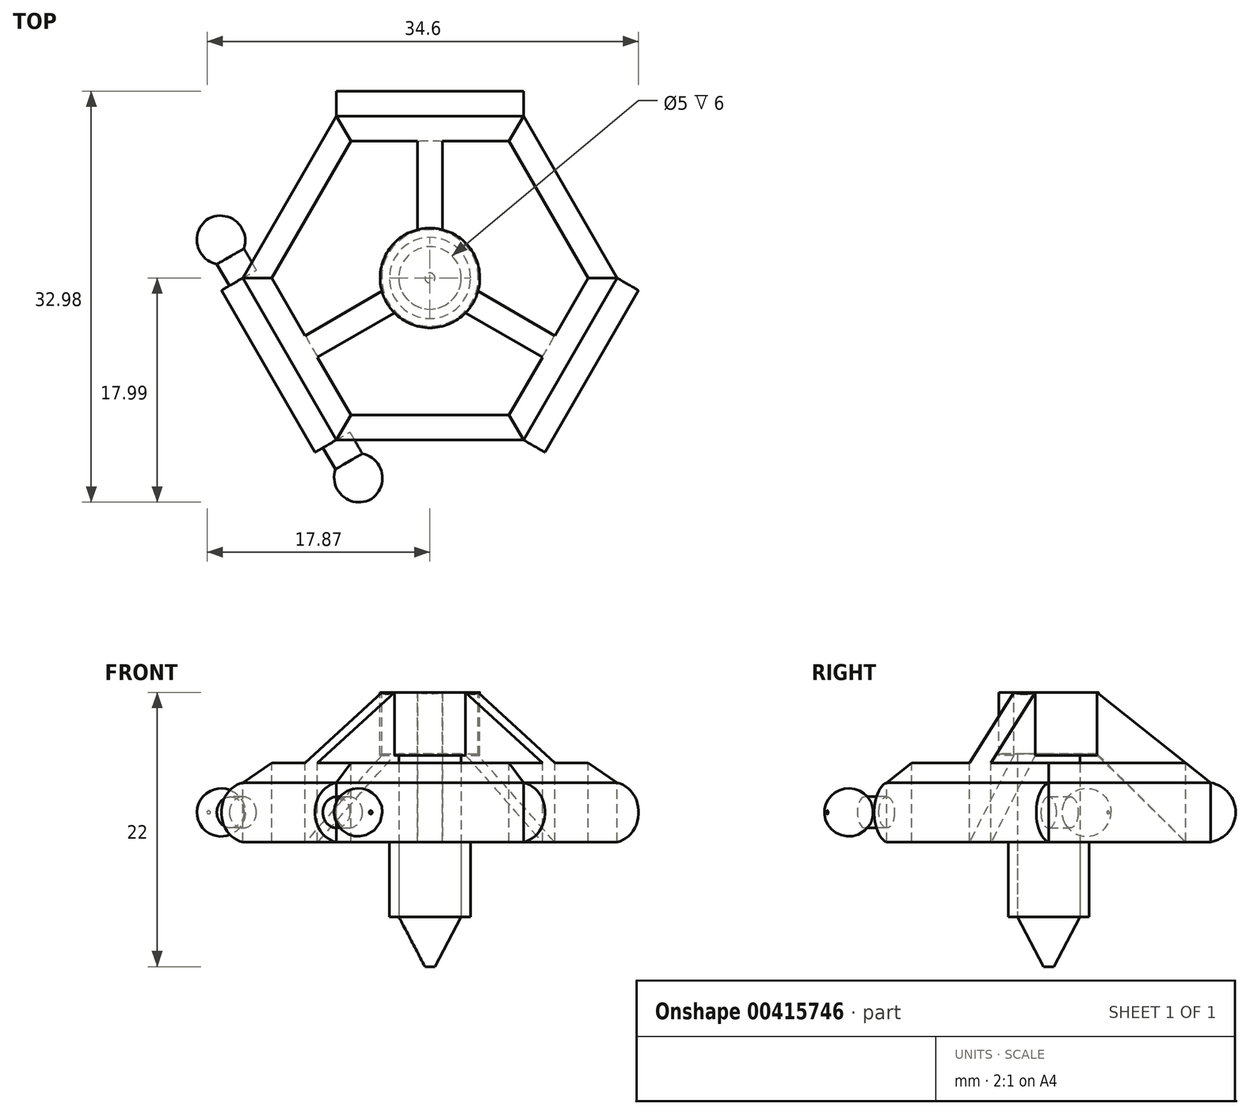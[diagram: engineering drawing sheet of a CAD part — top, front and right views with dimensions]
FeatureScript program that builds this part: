
annotation { "Feature Type Name" : "Feature", "Feature Type Description" : "" }
export const myFeature = defineFeature(function(context is Context, id is Id, definition is map)
    precondition{}
    {
        {
            var Q0;
            Q0=qCreatedBy(makeId("Top.planeOp"),FACE);
            var sketch = newSketch(context, id + "F0", { "sketchPlane" : qUnion([Q0])});
            skLineSegment(sketch, "E0", {"start": v(0, 25.98) * mm, "end": v(-22.5, -13) * mm, "construction": true});
            skLineSegment(sketch, "E1", {"start": v(-22.5, -13) * mm, "end": v(22.5, -13) * mm, "construction": true});
            skLineSegment(sketch, "E2", {"start": v(22.5, -13) * mm, "end": v(0, 25.98) * mm, "construction": true});
            skLineSegment(sketch, "E3", {"start": v(0, 0) * mm, "end": v(-22.5, -13) * mm, "construction": true});
            skLineSegment(sketch, "E4", {"start": v(0, 0) * mm, "end": v(22.5, -13) * mm, "construction": true});
            skLineSegment(sketch, "E5", {"start": v(0, 0) * mm, "end": v(0, 25.98) * mm, "construction": true});
            skCircle(sketch, "E6.cCircle", {"center": v(0, 0) * mm, "radius": 13 * mm, "construction": true});
            skLineSegment(sketch, "E6.0", {"start": v(7.5, -13) * mm, "end": v(-7.5, -13) * mm});
            skLineSegment(sketch, "E6.1", {"start": v(-7.5, -13) * mm, "end": v(-15, 0) * mm});
            skLineSegment(sketch, "E6.2", {"start": v(-15, 0) * mm, "end": v(-7.5, 13) * mm});
            skLineSegment(sketch, "E6.3", {"start": v(-7.5, 13) * mm, "end": v(7.5, 13) * mm});
            skLineSegment(sketch, "E6.4", {"start": v(7.5, 13) * mm, "end": v(15, 0) * mm});
            skLineSegment(sketch, "E6.5", {"start": v(15, 0) * mm, "end": v(7.5, -13) * mm});
            skPoint(sketch, "E6.0.midPoint", {"position": v(0, -13) * mm});
            skSolve(sketch);
        }
        {
            var Q0;
            Q0=makeQuery(id+"F0.imprint","IMPRINT",FACE,{"disambiguationData":[TD([[makeQuery(id+"F0.imprint","IMPRINT",EDGE,{"derivedFrom":sQuery(id+"F0.wireOp",EDGE,"E6.0")}),-1.0]])]});
            extrude(context, id + "F1", {"entities" : qUnion([Q0]), "depth" : 4.75 * mm});
        }
        {
            var Q0;
            Q0=makeQuery(id+"F1.opExtrude","CAP_FACE",FACE,{"disambiguationData":[OSD([sQuery(id+"F0.wireOp",EDGE,"E6.0"),sQuery(id+"F0.wireOp",EDGE,"E6.1"),sQuery(id+"F0.wireOp",EDGE,"E6.2"),sQuery(id+"F0.wireOp",EDGE,"E6.3"),sQuery(id+"F0.wireOp",EDGE,"E6.4"),sQuery(id+"F0.wireOp",EDGE,"E6.5")])],"isStart":false});
            cPlane(context, id + "F2", {"entities" : qUnion([Q0]), "cplaneType" : CPlaneType.OFFSET, "offset" : 10.33 * mm, "width" : 150 * mm, "height" : 150 * mm});
        }
        {
            var Q0;
            Q0=qCreatedBy(id+"F2.planeOp",FACE);
            var sketch = newSketch(context, id + "F3", { "sketchPlane" : qUnion([Q0])});
            skPoint(sketch, "E7", {"position": v(0, 0) * mm});
            skSolve(sketch);
        }
        {
            var Q1;
            Q1=makeQuery(id+"F1.opExtrude","CAP_FACE",FACE,{"disambiguationData":[OSD([sQuery(id+"F0.wireOp",EDGE,"E6.0"),sQuery(id+"F0.wireOp",EDGE,"E6.1"),sQuery(id+"F0.wireOp",EDGE,"E6.2"),sQuery(id+"F0.wireOp",EDGE,"E6.3"),sQuery(id+"F0.wireOp",EDGE,"E6.4"),sQuery(id+"F0.wireOp",EDGE,"E6.5")])],"isStart":false});
            var Q2;
            Q2=sQuery(id+"F3.wireOp",VERTEX,"E7");
            loft(context, id + "F4", {"operationType" : NewBodyOperationType.ADD, "sheetProfilesArray" : [{ "sheetProfileEntities" : qUnion([Q1]) }, { "sheetProfileEntities" : qUnion([Q2]) }]});
        }
        {
            var Q0;
            Q0=qCreatedBy(id+"F2.planeOp",FACE);
            var sketch = newSketch(context, id + "F5", { "sketchPlane" : qUnion([Q0])});
            skCircle(sketch, "E8", {"center": v(0, 0) * mm, "radius": 4 * mm});
            skLineSegment(sketch, "E9", {"start": v(-7.5, -13) * mm, "end": v(7.5, 13) * mm, "construction": true});
            skLineSegment(sketch, "E10", {"start": v(7.5, -13) * mm, "end": v(-7.5, 13) * mm, "construction": true});
            skLineSegment(sketch, "E11.bottom", {"start": v(-1, 11) * mm, "end": v(1, 11) * mm});
            skLineSegment(sketch, "E11.top", {"start": v(-1, 0) * mm, "end": v(1, 0) * mm});
            skLineSegment(sketch, "E11.left", {"start": v(-1, 11) * mm, "end": v(-1, 0) * mm});
            skLineSegment(sketch, "E11.right", {"start": v(1, 11) * mm, "end": v(1, 0) * mm});
            skLineSegment(sketch, "E12", {"start": v(-0.5, -0.87) * mm, "end": v(0.5, 0.87) * mm});
            skLineSegment(sketch, "E13", {"start": v(0.5, 0.87) * mm, "end": v(10.02, -4.63) * mm});
            skLineSegment(sketch, "E14", {"start": v(10.02, -4.63) * mm, "end": v(9.02, -6.36) * mm});
            skLineSegment(sketch, "E15", {"start": v(9.02, -6.36) * mm, "end": v(-0.5, -0.87) * mm});
            skLineSegment(sketch, "E16", {"start": v(-0.5, 0.87) * mm, "end": v(0.5, -0.87) * mm});
            skLineSegment(sketch, "E17", {"start": v(0.5, -0.87) * mm, "end": v(-9.02, -6.36) * mm});
            skLineSegment(sketch, "E18", {"start": v(-9.02, -6.36) * mm, "end": v(-10.02, -4.63) * mm});
            skLineSegment(sketch, "E19", {"start": v(-10.02, -4.63) * mm, "end": v(-0.5, 0.87) * mm});
            skCircle(sketch, "E20.cCircle", {"center": v(0, 0) * mm, "radius": 11 * mm, "construction": true});
            skLineSegment(sketch, "E20.0", {"start": v(-6.35, 11) * mm, "end": v(6.35, 11) * mm});
            skLineSegment(sketch, "E20.1", {"start": v(6.35, 11) * mm, "end": v(12.7, 0) * mm});
            skLineSegment(sketch, "E20.2", {"start": v(12.7, 0) * mm, "end": v(6.35, -11) * mm});
            skLineSegment(sketch, "E20.3", {"start": v(6.35, -11) * mm, "end": v(-6.35, -11) * mm});
            skLineSegment(sketch, "E20.4", {"start": v(-6.35, -11) * mm, "end": v(-12.7, 0) * mm});
            skLineSegment(sketch, "E20.5", {"start": v(-12.7, 0) * mm, "end": v(-6.35, 11) * mm});
            skPoint(sketch, "E20.0.midPoint", {"position": v(0, 11) * mm});
            skSolve(sketch);
        }
        {
            var Q0;
            {var subQ3=sQuery(id+"F5.wireOp",EDGE,"E20.5");Q0=makeQuery(id+"F5.imprint","IMPRINT",FACE,{"disambiguationData":[TD([[makeQuery(id+"F5.imprint","IMPRINT",EDGE,{"derivedFrom":subQ3}),-1.0]])]});}
            var Q1;
            {var subQ3=sQuery(id+"F5.wireOp",EDGE,"E20.1");Q1=makeQuery(id+"F5.imprint","IMPRINT",FACE,{"disambiguationData":[TD([[makeQuery(id+"F5.imprint","IMPRINT",EDGE,{"derivedFrom":subQ3}),-1.0]])]});}
            var Q2;
            {var subQ3=sQuery(id+"F5.wireOp",EDGE,"E20.3");Q2=makeQuery(id+"F5.imprint","IMPRINT",FACE,{"disambiguationData":[TD([[makeQuery(id+"F5.imprint","IMPRINT",EDGE,{"derivedFrom":subQ3}),-1.0]])]});}
            extrude(context, id + "F6", {"entities" : qUnion([Q0, Q1, Q2]), "operationType" : NewBodyOperationType.REMOVE, "oppositeDirection" : true, "depth" : 25 * mm});
        }
        {
            var Q0;
            {var subQ0=sQuery(id+"F5.wireOp",EDGE,"E11.left");var subQ1=sQuery(id+"F5.wireOp",EDGE,"E8");var subQ2=makeQuery(id+"F5.imprint","INTERSECT",VERTEX,{"derivedFrom":[subQ1,subQ0]});Q0=makeQuery(id+"F5.imprint","IMPRINT",FACE,{"disambiguationData":[TD([[makeQuery(id+"F5.imprint","IMPRINT",EDGE,{"disambiguationData":[TD([[subQ2,-1.0]])],"derivedFrom":subQ1}),1.0]])]});}
            var Q1;
            {var subQ1=sQuery(id+"F5.wireOp",EDGE,"E8");var subQ5=sQuery(id+"F5.wireOp",EDGE,"E11.left");var subQ6=makeQuery(id+"F5.imprint","INTERSECT",VERTEX,{"derivedFrom":[subQ1,subQ5]});Q1=makeQuery(id+"F5.imprint","IMPRINT",FACE,{"disambiguationData":[TD([[makeQuery(id+"F5.imprint","IMPRINT",EDGE,{"disambiguationData":[TD([[subQ6,1.0]])],"derivedFrom":subQ1}),1.0]])]});}
            var Q2;
            {var subQ0=sQuery(id+"F5.wireOp",EDGE,"E11.right");var subQ1=sQuery(id+"F5.wireOp",EDGE,"E8");var subQ2=makeQuery(id+"F5.imprint","INTERSECT",VERTEX,{"derivedFrom":[subQ1,subQ0]});Q2=makeQuery(id+"F5.imprint","IMPRINT",FACE,{"disambiguationData":[TD([[makeQuery(id+"F5.imprint","IMPRINT",EDGE,{"disambiguationData":[TD([[subQ2,1.0]])],"derivedFrom":subQ1}),1.0]])]});}
            var Q3;
            {var subQ8=sQuery(id+"F5.wireOp",EDGE,"E15");var subQ10=sQuery(id+"F5.wireOp",EDGE,"E8");var subQ13=makeQuery(id+"F5.imprint","INTERSECT",VERTEX,{"derivedFrom":[subQ10,subQ8]});Q3=makeQuery(id+"F5.imprint","IMPRINT",FACE,{"disambiguationData":[TD([[makeQuery(id+"F5.imprint","IMPRINT",EDGE,{"disambiguationData":[TD([[subQ13,-1.0]])],"derivedFrom":subQ10}),1.0]])]});}
            var Q4;
            {var subQ6=sQuery(id+"F5.wireOp",EDGE,"E8");var subQ11=sQuery(id+"F5.wireOp",EDGE,"E19");var subQ13=makeQuery(id+"F5.imprint","INTERSECT",VERTEX,{"derivedFrom":[subQ6,subQ11]});Q4=makeQuery(id+"F5.imprint","IMPRINT",FACE,{"disambiguationData":[TD([[makeQuery(id+"F5.imprint","IMPRINT",EDGE,{"disambiguationData":[TD([[subQ13,-1.0]])],"derivedFrom":subQ6}),1.0]])]});}
            var Q5;
            {var subQ0=sQuery(id+"F5.wireOp",EDGE,"E17");var subQ1=sQuery(id+"F5.wireOp",EDGE,"E8");var subQ2=makeQuery(id+"F5.imprint","INTERSECT",VERTEX,{"derivedFrom":[subQ1,subQ0]});Q5=makeQuery(id+"F5.imprint","IMPRINT",FACE,{"disambiguationData":[TD([[makeQuery(id+"F5.imprint","IMPRINT",EDGE,{"disambiguationData":[TD([[subQ2,-1.0]])],"derivedFrom":subQ1}),1.0]])]});}
            var Q6;
            {var subQ0=sQuery(id+"F5.wireOp",EDGE,"E11.right");var subQ1=sQuery(id+"F5.wireOp",EDGE,"E11.top");var subQ2=makeQuery(id+"F5.imprint","INTERSECT",VERTEX,{"derivedFrom":[subQ1,subQ0]});Q6=makeQuery(id+"F5.imprint","IMPRINT",FACE,{"disambiguationData":[TD([[makeQuery(id+"F5.imprint","IMPRINT",EDGE,{"disambiguationData":[TD([[subQ2,1.0]])],"derivedFrom":subQ0}),-1.0]])]});}
            var Q7;
            {var subQ0=sQuery(id+"F5.wireOp",EDGE,"E11.left");var subQ1=sQuery(id+"F5.wireOp",EDGE,"E11.top");var subQ2=makeQuery(id+"F5.imprint","INTERSECT",VERTEX,{"derivedFrom":[subQ1,subQ0]});Q7=makeQuery(id+"F5.imprint","IMPRINT",FACE,{"disambiguationData":[TD([[makeQuery(id+"F5.imprint","IMPRINT",EDGE,{"disambiguationData":[TD([[subQ2,1.0]])],"derivedFrom":subQ0}),1.0]])]});}
            var Q8;
            {var subQ0=sQuery(id+"F5.wireOp",EDGE,"E15");var subQ1=sQuery(id+"F5.wireOp",EDGE,"E12");var subQ2=makeQuery(id+"F5.imprint","INTERSECT",VERTEX,{"derivedFrom":[subQ1,subQ0]});Q8=makeQuery(id+"F5.imprint","IMPRINT",FACE,{"disambiguationData":[TD([[makeQuery(id+"F5.imprint","IMPRINT",EDGE,{"disambiguationData":[TD([[subQ2,1.0]])],"derivedFrom":subQ0}),-1.0]])]});}
            var Q9;
            Q9=sQuery(id+"F5.wireOp",EDGE,"E8");
            extrude(context, id + "F7", {"entities" : qUnion([Q0, Q1, Q2, Q3, Q4, Q5, Q6, Q7, Q8]), "operationType" : NewBodyOperationType.ADD, "surfaceEntities" : qUnion([Q9]), "oppositeDirection" : true, "depth" : 4 * mm});
        }
        {
            var Q0;
            Q0=makeQuery(id+"F7.opExtrude","CAP_FACE",FACE,{"disambiguationData":[OSD([sQuery(id+"F5.wireOp",EDGE,"E8")])],"isStart":true});
            var Q1;
            {var subQ0=sQuery(id+"F5.wireOp",EDGE,"E15");var subQ1=sQuery(id+"F5.wireOp",EDGE,"E8");Q1=makeQuery(id+"F6.boolean.opBoolean","INTERSECT",VERTEX,{"derivedFrom":[makeQuery(id+"F4.opLoft","SWEPT_FACE",FACE,{"disambiguationData":[OSD([sQuery(id+"F0.wireOp",EDGE,"E6.0"),sQuery(id+"F0.wireOp",EDGE,"E6.4"),sQuery(id+"F0.wireOp",EDGE,"E6.5")])]}),makeQuery(id+"F6.opExtrude","SWEPT_FACE",FACE,{"disambiguationData":[OSD([subQ1]),TDD([makeQuery(id+"F5.imprint","IMPRINT",EDGE,{"disambiguationData":[TD([[makeQuery(id+"F5.imprint","INTERSECT",VERTEX,{"derivedFrom":[subQ1,sQuery(id+"F5.wireOp",EDGE,"E17")]}),-1.0]])],"derivedFrom":subQ1})])]}),makeQuery(id+"F6.opExtrude","SWEPT_FACE",FACE,{"disambiguationData":[OSD([subQ0])]})]});}
            extrude(context, id + "F8", {"entities" : qUnion([Q0]), "operationType" : NewBodyOperationType.REMOVE, "endBound" : BoundingType.UP_TO_VERTEX, "oppositeDirection" : true, "endBoundEntityVertex" : qUnion([Q1]), "depth" : 3 * mm});
        }
        {
            var Q0;
            Q0=qCreatedBy(id+"F2.planeOp",FACE);
            cPlane(context, id + "F9", {"entities" : qUnion([Q0]), "cplaneType" : CPlaneType.OFFSET, "offset" : 8 * mm, "oppositeDirection" : true, "width" : 150 * mm, "height" : 150 * mm});
        }
        {
            var Q0;
            Q0=qCreatedBy(id+"F9.planeOp",FACE);
            var sketch = newSketch(context, id + "F10", { "sketchPlane" : qUnion([Q0])});
            skCircle(sketch, "E21", {"center": v(0, 0) * mm, "radius": 4 * mm});
            skSolve(sketch);
        }
        {
            var Q0;
            Q0=makeQuery(id+"F6.boolean.opBoolean","COPY",FACE,{"derivedFrom":makeQuery(id+"F6.opExtrude","SWEPT_FACE",FACE,{"disambiguationData":[OSD([sQuery(id+"F5.wireOp",EDGE,"E11.left")])]})});
            cPlane(context, id + "F11", {"entities" : qUnion([Q0]), "cplaneType" : CPlaneType.OFFSET, "offset" : 1 * mm, "oppositeDirection" : true, "width" : 150 * mm, "height" : 150 * mm});
        }
        {
            var Q0;
            Q0=qCreatedBy(id+"F11.planeOp",FACE);
            var sketch = newSketch(context, id + "F12", { "sketchPlane" : qUnion([Q0])});
            skLineSegment(sketch, "E22", {"start": v(-11, 0) * mm, "end": v(-3.87, 7.08) * mm});
            skLineSegment(sketch, "E23", {"start": v(-3.87, 7.08) * mm, "end": v(0, 7.08) * mm});
            skLineSegment(sketch, "E24", {"start": v(0, 7.08) * mm, "end": v(0, 0) * mm});
            skLineSegment(sketch, "E25", {"start": v(0, 0) * mm, "end": v(-11, 0) * mm});
            skSolve(sketch);
        }
        {
            var Q0;
            Q0 = qSketchRegion(id + "F12", true);
            var Q1;
            Q1=sQuery(id+"F12.wireOp",EDGE,"E24");
            revolve(context, id + "F13", {"operationType" : NewBodyOperationType.REMOVE, "entities" : qUnion([Q0]), "axis" : qUnion([Q1]), "revolveType" : RevolveType.FULL, "oppositeDirection" : true});
        }
        {
            var Q0;
            Q0=makeQuery(id+"F1.opExtrude","SWEPT_EDGE",EDGE,{"disambiguationData":[OSD([sQuery(id+"F0.wireOp",EDGE,"E6.0"),sQuery(id+"F0.wireOp",EDGE,"E6.1")])]});
            cPoint(context, id + "F14", {"entities" : qUnion([Q0]), "parameter" : 0.5});
        }
        {
            var Q0;
            {var subQ0=sQuery(id+"F0.wireOp",EDGE,"E6.1");Q0=makeQuery(id+"F4.boolean.opBoolean","MERGE",EDGE,{"derivedFrom":[makeQuery(id+"F1.opExtrude","CAP_EDGE",EDGE,{"disambiguationData":[OSD([subQ0])],"isStart":false}),makeQuery(id+"F4.opLoft","MID_CAP_EDGE",EDGE,{"disambiguationData":[OSD([sQuery(id+"F0.wireOp",EDGE,"E6.0"),subQ0,sQuery(id+"F0.wireOp",EDGE,"E6.2")])],"capPos":0.0})]});}
            var Q1;
            Q1 = qCreatedBy(id + "F14" ,VERTEX);
            cPlane(context, id + "F15", {"entities" : qUnion([Q0, Q1]), "cplaneType" : CPlaneType.LINE_POINT, "offset" : 25 * mm, "width" : 150 * mm, "height" : 150 * mm});
        }
        {
            var Q0;
            Q0=qCreatedBy(id+"F15.planeOp",FACE);
            var sketch = newSketch(context, id + "F16", { "sketchPlane" : qUnion([Q0])});
            skArc(sketch, "E26", {"start": v(13, 0) * mm, "mid": v(15, 2.38) * mm, "end": v(13, 4.75) * mm});
            skLineSegment(sketch, "E27", {"start": v(13, 0) * mm, "end": v(13, 4.75) * mm});
            skSolve(sketch);
        }
        {
            var Q0;
            Q0=makeQuery(id+"F16.imprint","IMPRINT",FACE,{"disambiguationData":[TD([[makeQuery(id+"F16.imprint","IMPRINT",EDGE,{"derivedFrom":sQuery(id+"F16.wireOp",EDGE,"E26")}),1.0]])]});
            var Q1;
            {var subQ0=sQuery(id+"F0.wireOp",EDGE,"E6.2");var subQ1=sQuery(id+"F0.wireOp",EDGE,"E6.1");Q1=makeQuery(id+"F4.boolean.opBoolean","MERGE",VERTEX,{"derivedFrom":[makeQuery(id+"F1.opExtrude","CAP_VERTEX",VERTEX,{"disambiguationData":[OSD([subQ1,subQ0])],"isStart":false}),makeQuery(id+"F4.opLoft","MID_CAP_VERTEX",VERTEX,{"disambiguationData":[OSD([subQ1,subQ0])],"capPos":0.0})]});}
            extrude(context, id + "F17", {"entities" : qUnion([Q0]), "endBound" : BoundingType.UP_TO_VERTEX, "endBoundEntityVertex" : qUnion([Q1]), "depth" : 25 * mm});
        }
        {
            var Q0;
            Q0=makeQuery(id+"F17.opExtrude","CAP_FACE",FACE,{"disambiguationData":[OSD([sQuery(id+"F16.wireOp",EDGE,"E26"),sQuery(id+"F16.wireOp",EDGE,"E27")])],"isStart":true});
            cPlane(context, id + "F18", {"entities" : qUnion([Q0]), "cplaneType" : CPlaneType.OFFSET, "offset" : 2 * mm, "width" : 150 * mm, "height" : 150 * mm});
        }
        {
            var Q0;
            Q0=qCreatedBy(id+"F18.planeOp",FACE);
            var sketch = newSketch(context, id + "F19", { "sketchPlane" : qUnion([Q0])});
            skCircle(sketch, "E28", {"center": v(-13, 2.38) * mm, "radius": 1.25 * mm});
            skLineSegment(sketch, "E29", {"start": v(-14.24, 2.38) * mm, "end": v(-11.74, 2.38) * mm, "construction": true});
            skSolve(sketch);
        }
        {
            var Q0;
            Q0=makeQuery(id+"F19.imprint","IMPRINT",FACE,{"disambiguationData":[TD([[makeQuery(id+"F19.imprint","IMPRINT",EDGE,{"derivedFrom":sQuery(id+"F19.wireOp",EDGE,"E28")}),1.0]])]});
            var Q1;
            Q1=makeQuery(id+"F17.opExtrude","CAP_FACE",FACE,{"disambiguationData":[OSD([sQuery(id+"F16.wireOp",EDGE,"E26"),sQuery(id+"F16.wireOp",EDGE,"E27")])],"isStart":true});
            extrude(context, id + "F20", {"entities" : qUnion([Q0]), "endBound" : BoundingType.UP_TO_SURFACE, "oppositeDirection" : true, "endBoundEntityFace" : qUnion([Q1]), "depth" : 25 * mm});
        }
        {
            var Q0;
            {var subQ0=sQuery(id+"F0.wireOp",EDGE,"E6.1");var subQ1=sQuery(id+"F0.wireOp",EDGE,"E6.0");Q0=makeQuery(id+"F4.boolean.opBoolean","MERGE",VERTEX,{"derivedFrom":[makeQuery(id+"F1.opExtrude","CAP_VERTEX",VERTEX,{"disambiguationData":[OSD([subQ1,subQ0])],"isStart":false}),makeQuery(id+"F4.opLoft","MID_CAP_VERTEX",VERTEX,{"disambiguationData":[OSD([subQ1,subQ0])],"capPos":0.0})]});}
            var Q1;
            Q1=makeQuery(id+"F1.opExtrude","CAP_VERTEX",VERTEX,{"disambiguationData":[OSD([sQuery(id+"F0.wireOp",EDGE,"E6.0"),sQuery(id+"F0.wireOp",EDGE,"E6.1")])],"isStart":true});
            cPlane(context, id + "F21", {"entities" : qUnion([Q0, Q1]), "cplaneType" : CPlaneType.MID_PLANE, "offset" : 25 * mm, "width" : 150 * mm, "height" : 150 * mm});
        }
        {
            var Q0;
            Q0=qCreatedBy(id+"F21.planeOp",FACE);
            var sketch = newSketch(context, id + "F22", { "sketchPlane" : qUnion([Q0])});
            skLineSegment(sketch, "E30", {"start": v(-7.58, 15.35) * mm, "end": v(-6.5, 14.72) * mm});
            skLineSegment(sketch, "E31", {"start": v(-6.5, 14.72) * mm, "end": v(-4.75, 17.75) * mm});
            skLineSegment(sketch, "E32", {"start": v(-4.75, 17.75) * mm, "end": v(-4.75, 17.75) * mm});
            skArc(sketch, "E33", {"start": v(-4.75, 17.75) * mm, "mid": v(-6.98, 17.51) * mm, "end": v(-7.58, 15.35) * mm});
            skLineSegment(sketch, "E34", {"start": v(-6.5, 14.72) * mm, "end": v(-17.06, -3.57) * mm, "construction": true});
            skLineSegment(sketch, "E35", {"start": v(0, 0) * mm, "end": v(-15.66, 9.04) * mm, "construction": true});
            skSolve(sketch);
        }
        {
            var Q0;
            Q0=makeQuery(id+"F22.imprint","IMPRINT",FACE,{"disambiguationData":[TD([[makeQuery(id+"F22.imprint","IMPRINT",EDGE,{"derivedFrom":sQuery(id+"F22.wireOp",EDGE,"E30")}),1.0]])]});
            var Q1;
            Q1=sQuery(id+"F19.wireOp",EDGE,"E28");
            revolve(context, id + "F23", {"operationType" : NewBodyOperationType.ADD, "entities" : qUnion([Q0]), "axis" : qUnion([Q1]), "revolveType" : RevolveType.FULL});
        }
        {
            var Q0;
            Q0=makeQuery(id+"F20.opExtrude","SWEPT_BODY",BODY,{"disambiguationData":[OSD([sQuery(id+"F19.wireOp",EDGE,"E28")])]});
            var Q1;
            Q1=sQuery(id+"F22.wireOp",EDGE,"E35");
            transform(context, id + "F24", {"entities" : qUnion([Q0]), "transformType" : TransformType.ROTATION, "transformAxis" : qUnion([Q1]), "angle" : 180 * degree, "makeCopy" : true});
        }
        {
            var Q0;
            Q0=sQuery(id+"F5.wireOp",EDGE,"E12");
            cPoint(context, id + "F25", {"entities" : qUnion([Q0]), "parameter" : 0.5});
        }
        {
            var Q0;
            Q0=qCreatedBy(makeId("Origin.pointOp"),VERTEX);
            var Q1;
            Q1=sQuery(id+"F22.wireOp",VERTEX,"E35.end");
            var Q2;
            Q2 = qCreatedBy(id + "F25" ,VERTEX);
            cPlane(context, id + "F26", {"entities" : qUnion([Q0, Q1, Q2]), "cplaneType" : CPlaneType.THREE_POINT, "offset" : 25 * mm, "width" : 150 * mm, "height" : 150 * mm});
        }
        {
            var Q0;
            Q0=qCreatedBy(id+"F26.planeOp",FACE);
            var sketch = newSketch(context, id + "F27", { "sketchPlane" : qUnion([Q0])});
            skLineSegment(sketch, "E36", {"start": v(0, 15.08) * mm, "end": v(0, 0) * mm, "construction": true});
            skSolve(sketch);
        }
        {
            var Q0;
            Q0=makeQuery(id+"F17.opExtrude","SWEPT_BODY",BODY,{"disambiguationData":[OSD([sQuery(id+"F16.wireOp",EDGE,"E26"),sQuery(id+"F16.wireOp",EDGE,"E27")])]});
            var Q1;
            Q1=sQuery(id+"F27.wireOp",EDGE,"E36");
            transform(context, id + "F28", {"entities" : qUnion([Q0]), "transformType" : TransformType.ROTATION, "transformAxis" : qUnion([Q1]), "angle" : 120 * degree, "makeCopy" : true});
        }
        {
            var Q0;
            Q0=makeQuery(id+"F28.opPattern","COPY",BODY,{"derivedFrom":makeQuery(id+"F17.opExtrude","SWEPT_BODY",BODY,{"disambiguationData":[OSD([sQuery(id+"F16.wireOp",EDGE,"E26"),sQuery(id+"F16.wireOp",EDGE,"E27")])]}),"instanceName":"1"});
            var Q1;
            Q1=sQuery(id+"F27.wireOp",EDGE,"E36");
            transform(context, id + "F29", {"entities" : qUnion([Q0]), "transformType" : TransformType.ROTATION, "transformAxis" : qUnion([Q1]), "angle" : 120 * degree, "makeCopy" : true});
        }
        {
            var Q0;
            Q0=makeQuery(id+"F1.opExtrude","CAP_FACE",FACE,{"disambiguationData":[OSD([sQuery(id+"F0.wireOp",EDGE,"E6.0"),sQuery(id+"F0.wireOp",EDGE,"E6.1"),sQuery(id+"F0.wireOp",EDGE,"E6.2"),sQuery(id+"F0.wireOp",EDGE,"E6.3"),sQuery(id+"F0.wireOp",EDGE,"E6.4"),sQuery(id+"F0.wireOp",EDGE,"E6.5")])],"isStart":true});
            cPlane(context, id + "F30", {"entities" : qUnion([Q0]), "cplaneType" : CPlaneType.OFFSET, "offset" : 10 * mm, "width" : 150 * mm, "height" : 150 * mm});
        }
        {
            var Q0;
            Q0=makeQuery(id+"F1.opExtrude","CAP_FACE",FACE,{"disambiguationData":[OSD([sQuery(id+"F0.wireOp",EDGE,"E6.0"),sQuery(id+"F0.wireOp",EDGE,"E6.1"),sQuery(id+"F0.wireOp",EDGE,"E6.2"),sQuery(id+"F0.wireOp",EDGE,"E6.3"),sQuery(id+"F0.wireOp",EDGE,"E6.4"),sQuery(id+"F0.wireOp",EDGE,"E6.5")])],"isStart":true});
            cPlane(context, id + "F31", {"entities" : qUnion([Q0]), "cplaneType" : CPlaneType.OFFSET, "offset" : 6 * mm, "width" : 150 * mm, "height" : 150 * mm});
        }
        {
            var Q0;
            Q0=qCreatedBy(id+"F31.planeOp",FACE);
            var sketch = newSketch(context, id + "F32", { "sketchPlane" : qUnion([Q0])});
            skCircle(sketch, "E37", {"center": v(0, 0) * mm, "radius": 2.5 * mm});
            skCircle(sketch, "E38", {"center": v(0, 0) * mm, "radius": 3.25 * mm});
            skSolve(sketch);
        }
        {
            var Q0;
            Q0=makeQuery(id+"F32.imprint","IMPRINT",FACE,{"disambiguationData":[TD([[makeQuery(id+"F32.imprint","IMPRINT",EDGE,{"derivedFrom":sQuery(id+"F32.wireOp",EDGE,"E37")}),1.0]])]});
            var Q1;
            Q1=makeQuery(id+"F13.boolean.opBoolean","COPY",FACE,{"derivedFrom":makeQuery(id+"F13.opRevolve","SWEPT_FACE",FACE,{"disambiguationData":[OSD([sQuery(id+"F12.wireOp",EDGE,"E23")])]})});
            extrude(context, id + "F33", {"entities" : qUnion([Q0]), "endBound" : BoundingType.UP_TO_SURFACE, "oppositeDirection" : true, "endBoundEntityFace" : qUnion([Q1]), "depth" : 25 * mm});
        }
        {
            var Q0;
            Q0=qCreatedBy(id+"F30.planeOp",FACE);
            var sketch = newSketch(context, id + "F34", { "sketchPlane" : qUnion([Q0])});
            skCircle(sketch, "E39", {"center": v(0, 0) * mm, "radius": 0.4 * mm});
            skSolve(sketch);
        }
        {
            var Q1;
            Q1=makeQuery(id+"F33.opExtrude","CAP_FACE",FACE,{"disambiguationData":[OSD([sQuery(id+"F32.wireOp",EDGE,"E37")])],"isStart":true});
            var Q2;
            Q2=makeQuery(id+"F34.imprint","IMPRINT",FACE,{"disambiguationData":[TD([[makeQuery(id+"F34.imprint","IMPRINT",EDGE,{"derivedFrom":sQuery(id+"F34.wireOp",EDGE,"E39")}),1.0]])]});
            loft(context, id + "F35", {"operationType" : NewBodyOperationType.ADD, "sheetProfilesArray" : [{ "sheetProfileEntities" : qUnion([Q1]) }, { "sheetProfileEntities" : qUnion([Q2]) }]});
        }
        {
            var Q0;
            Q0=makeQuery(id+"F32.imprint","IMPRINT",FACE,{"disambiguationData":[TD([[makeQuery(id+"F32.imprint","IMPRINT",EDGE,{"derivedFrom":sQuery(id+"F32.wireOp",EDGE,"E37")}),-1.0]])]});
            extrude(context, id + "F36", {"entities" : qUnion([Q0]), "oppositeDirection" : true, "depth" : 6 * mm});
        }
    });
